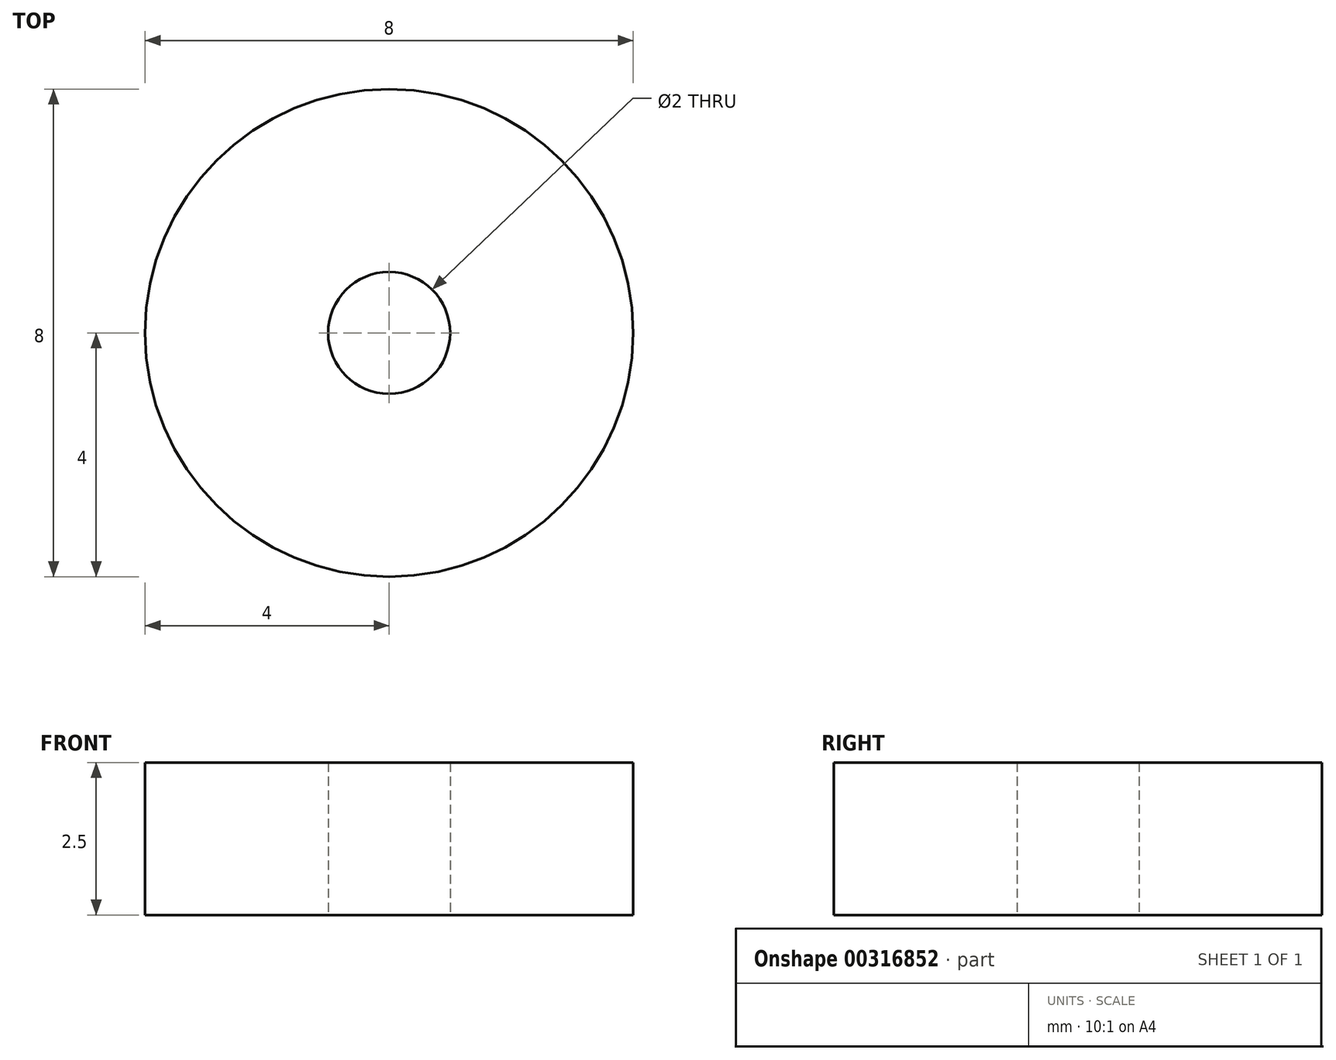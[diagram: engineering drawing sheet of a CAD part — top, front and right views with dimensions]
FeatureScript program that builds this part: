
annotation { "Feature Type Name" : "Feature", "Feature Type Description" : "" }
export const myFeature = defineFeature(function(context is Context, id is Id, definition is map)
    precondition{}
    {
        {
            var Q0;
            Q0=qCreatedBy(makeId("Top.planeOp"),FACE);
            var sketch = newSketch(context, id + "F0", { "sketchPlane" : qUnion([Q0])});
            skCircle(sketch, "E0", {"center": v(0, 0) * mm, "radius": 1 * mm});
            skCircle(sketch, "E1", {"center": v(0, 0) * mm, "radius": 4 * mm});
            skSolve(sketch);
        }
        {
            var Q0;
            Q0=makeQuery(id+"F0.imprint","IMPRINT",FACE,{"disambiguationData":[TD([[makeQuery(id+"F0.imprint","IMPRINT",EDGE,{"derivedFrom":sQuery(id+"F0.wireOp",EDGE,"E0")}),-1.0]])]});
            extrude(context, id + "F1", {"entities" : qUnion([Q0]), "depth" : 2.5 * mm});
        }
    });
